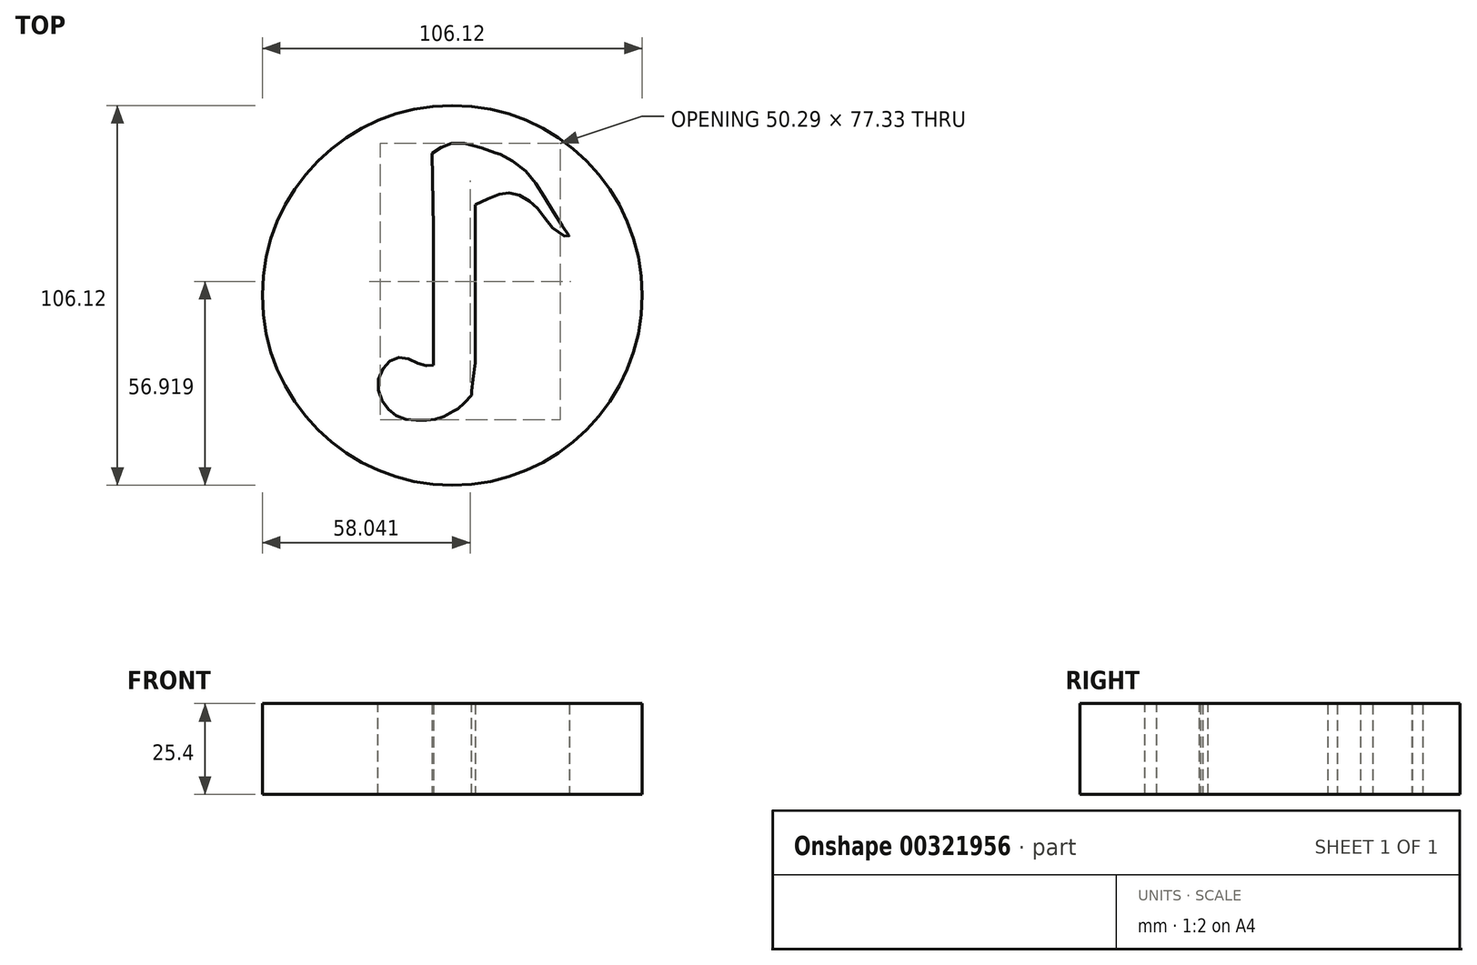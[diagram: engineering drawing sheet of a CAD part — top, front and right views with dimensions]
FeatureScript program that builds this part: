
annotation { "Feature Type Name" : "Feature", "Feature Type Description" : "" }
export const myFeature = defineFeature(function(context is Context, id is Id, definition is map)
    precondition{}
    {
        {
            var Q0;
            Q0=qCreatedBy(makeId("Top.planeOp"),FACE);
            var sketch = newSketch(context, id + "F0", { "sketchPlane" : qUnion([Q0])});
            skCircle(sketch, "E0", {"center": v(0, 0) * mm, "radius": 53.06 * mm});
            skLineSegment(sketch, "E1", {"start": v(-5.21, 18.77) * mm, "end": v(-5.21, -19.47) * mm});
            skLineSegment(sketch, "E2", {"start": v(6.41, 25.27) * mm, "end": v(6.41, -18.87) * mm});
            skLineSegment(sketch, "E3", {"start": v(-5.6, 39.66) * mm, "end": v(-5.21, 18.77) * mm});
            skFitSpline(sketch, "E4", {"points": [v(-5.6, 39.66) * mm, v(-1.67, 42.02) * mm, v(4.64, 42.22) * mm, v(12.52, 39.66) * mm, v(12.72, 39.66) * mm, v(18.63, 36.3) * mm, v(24.94, 28.82) * mm, v(30.65, 19.55) * mm, v(32.62, 16.2) * mm, v(28.1, 18.77) * mm, v(24.35, 23.7) * mm, v(20.8, 26.85) * mm, v(16.46, 28.62) * mm, v(12.72, 28.03) * mm, v(6.41, 25.27) * mm], "startDerivative": vector(57.37, 41.36) * mm, "endDerivative": vector(-83.66, -39.26) * mm});
            skFitSpline(sketch, "E5", {"points": [v(-5.21, -19.47) * mm, v(-8.56, -19.47) * mm, v(-13.88, -17.3) * mm, v(-18.61, -19.47) * mm, v(-20.78, -25.77) * mm, v(-18.02, -31.68) * mm, v(-13.1, -34.64) * mm, v(-6.99, -34.84) * mm, v(-2.65, -34.05) * mm, v(1.49, -31.68) * mm, v(1.68, -31.68) * mm, v(5.43, -27.74) * mm, v(5.43, -27.54) * mm, v(6.41, -18.87) * mm], "startDerivative": vector(-46.99, -8.29) * mm, "endDerivative": vector(15.4, 110.87) * mm});
            skSolve(sketch);
        }
        {
            var Q0;
            Q0=makeQuery(id+"F0.imprint","IMPRINT",FACE,{"disambiguationData":[TD([[makeQuery(id+"F0.imprint","IMPRINT",EDGE,{"derivedFrom":sQuery(id+"F0.wireOp",EDGE,"E0")}),1.0]])]});
            extrude(context, id + "F1", {"entities" : qUnion([Q0]), "depth" : 25.4 * mm});
        }
    });
